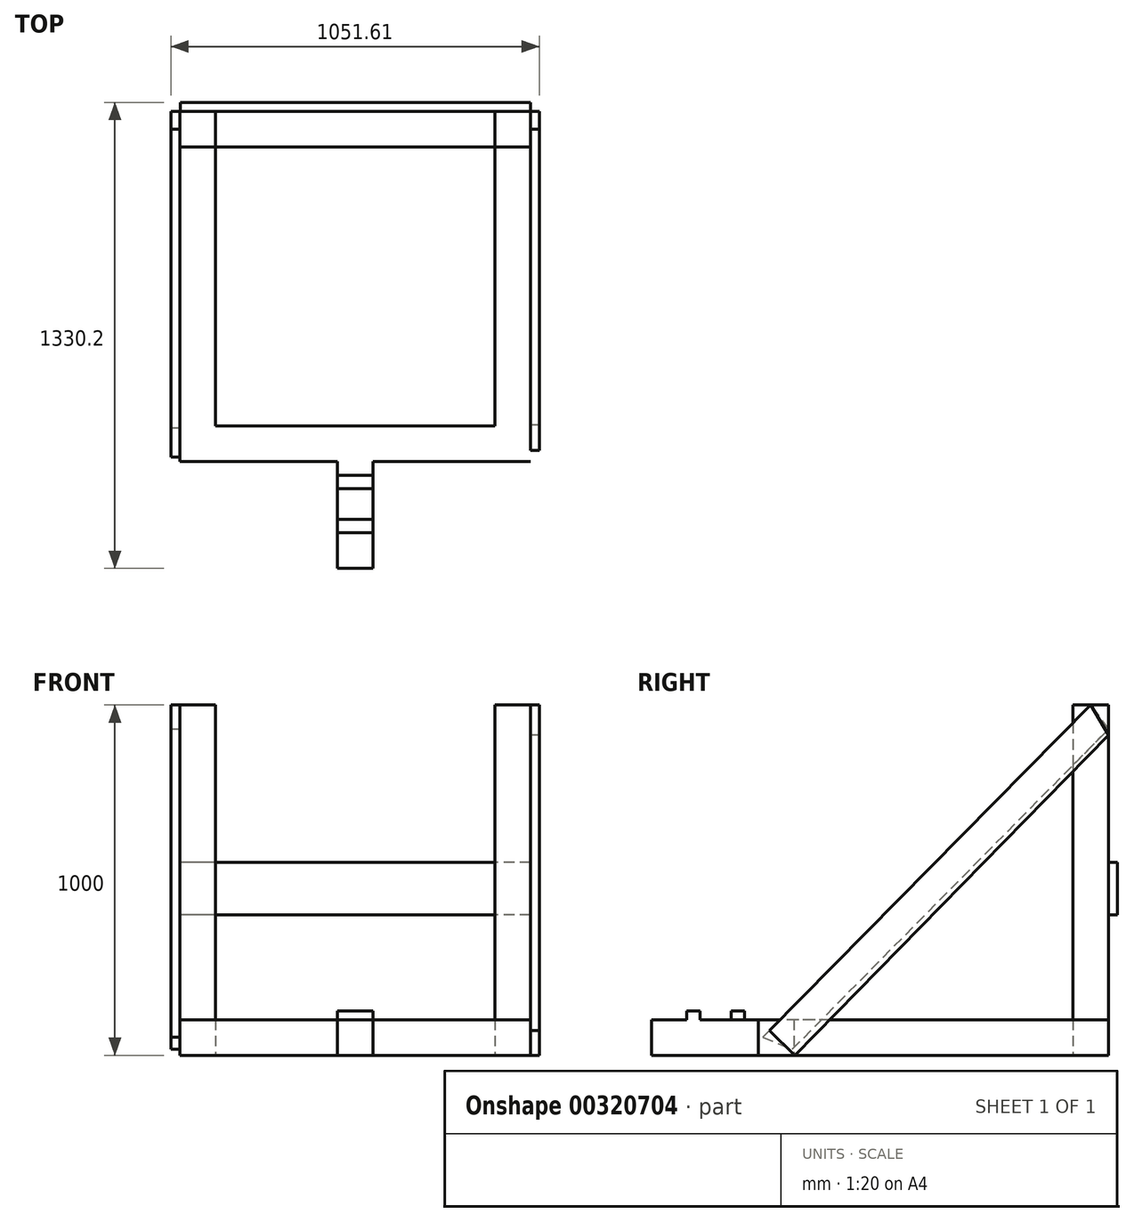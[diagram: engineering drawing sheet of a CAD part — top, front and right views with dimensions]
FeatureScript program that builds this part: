
annotation { "Feature Type Name" : "Feature", "Feature Type Description" : "" }
export const myFeature = defineFeature(function(context is Context, id is Id, definition is map)
    precondition{}
    {
        {
            var Q0;
            Q0=qCreatedBy(makeId("Top.planeOp"),FACE);
            var sketch = newSketch(context, id + "F0", { "sketchPlane" : qUnion([Q0])});
            skLineSegment(sketch, "E0.bottom", {"start": v(-1101.6, 500) * mm, "end": v(-1000, 500) * mm});
            skLineSegment(sketch, "E0.top", {"start": v(-1101.6, -500) * mm, "end": v(-1000, -500) * mm});
            skLineSegment(sketch, "E0.left", {"start": v(-1101.6, 500) * mm, "end": v(-1101.6, -500) * mm});
            skLineSegment(sketch, "E0.right", {"start": v(-1000, 500) * mm, "end": v(-1000, -500) * mm});
            skSolve(sketch);
        }
        {
            var Q0;
            Q0 = qSketchRegion(id + "F0", true);
            extrude(context, id + "F1", {"entities" : qUnion([Q0]), "depth" : 101.6 * mm});
        }
        {
            var Q0;
            Q0=makeQuery(id+"F1.opExtrude","SWEPT_FACE",FACE,{"disambiguationData":[OSD([sQuery(id+"F0.wireOp",EDGE,"E0.right")])]});
            cPlane(context, id + "F2", {"entities" : qUnion([Q0]), "cplaneType" : CPlaneType.OFFSET, "offset" : 0 * mm, "width" : 152.4 * mm, "height" : 152.4 * mm});
        }
        {
            var Q0;
            Q0=qCreatedBy(id+"F2.planeOp",FACE);
            var sketch = newSketch(context, id + "F3", { "sketchPlane" : qUnion([Q0])});
            skLineSegment(sketch, "E1.bottom", {"start": v(500, 101.6) * mm, "end": v(398.4, 101.6) * mm});
            skLineSegment(sketch, "E1.top", {"start": v(500, 0) * mm, "end": v(398.4, 0) * mm});
            skLineSegment(sketch, "E1.left", {"start": v(500, 101.6) * mm, "end": v(500, 0) * mm});
            skLineSegment(sketch, "E1.right", {"start": v(398.4, 101.6) * mm, "end": v(398.4, 0) * mm});
            skSolve(sketch);
        }
        {
            var Q0;
            Q0 = qSketchRegion(id + "F3", true);
            extrude(context, id + "F4", {"entities" : qUnion([Q0]), "operationType" : NewBodyOperationType.ADD, "depth" : 796.8 * mm});
        }
        {
            var Q0;
            Q0=makeQuery(id+"F4.opExtrude","CAP_FACE",FACE,{"disambiguationData":[OSD([sQuery(id+"F3.wireOp",EDGE,"E1.bottom"),sQuery(id+"F3.wireOp",EDGE,"E1.top"),sQuery(id+"F3.wireOp",EDGE,"E1.left"),sQuery(id+"F3.wireOp",EDGE,"E1.right")])],"isStart":false});
            cPlane(context, id + "F5", {"entities" : qUnion([Q0]), "cplaneType" : CPlaneType.OFFSET, "offset" : 0 * mm, "width" : 152.4 * mm, "height" : 152.4 * mm});
        }
        {
            var Q0;
            Q0=qCreatedBy(id+"F5.planeOp",FACE);
            var sketch = newSketch(context, id + "F6", { "sketchPlane" : qUnion([Q0])});
            skLineSegment(sketch, "E2.bottom", {"start": v(500, 101.6) * mm, "end": v(-500, 101.6) * mm});
            skLineSegment(sketch, "E2.top", {"start": v(500, 0) * mm, "end": v(-500, 0) * mm});
            skLineSegment(sketch, "E2.left", {"start": v(500, 101.6) * mm, "end": v(500, 0) * mm});
            skLineSegment(sketch, "E2.right", {"start": v(-500, 101.6) * mm, "end": v(-500, 0) * mm});
            skSolve(sketch);
        }
        {
            var Q0;
            Q0=makeQuery(id+"F6.imprint","IMPRINT",FACE,{"disambiguationData":[TD([[makeQuery(id+"F6.imprint","IMPRINT",EDGE,{"derivedFrom":sQuery(id+"F6.wireOp",EDGE,"E2.bottom")}),1.0]])]});
            extrude(context, id + "F7", {"entities" : qUnion([Q0]), "operationType" : NewBodyOperationType.ADD, "depth" : 101.6 * mm});
        }
        {
            var Q0;
            Q0=makeQuery(id+"F1.opExtrude","SWEPT_FACE",FACE,{"disambiguationData":[OSD([sQuery(id+"F0.wireOp",EDGE,"E0.right")])]});
            var sketch = newSketch(context, id + "F8", { "sketchPlane" : qUnion([Q0])});
            skLineSegment(sketch, "E3.bottom", {"start": v(-500, 101.6) * mm, "end": v(-398.4, 101.6) * mm});
            skLineSegment(sketch, "E3.top", {"start": v(-500, 0) * mm, "end": v(-398.4, 0) * mm});
            skLineSegment(sketch, "E3.left", {"start": v(-500, 101.6) * mm, "end": v(-500, 0) * mm});
            skLineSegment(sketch, "E3.right", {"start": v(-398.4, 101.6) * mm, "end": v(-398.4, 0) * mm});
            skSolve(sketch);
        }
        {
            var Q0;
            Q0 = qSketchRegion(id + "F8", true);
            extrude(context, id + "F9", {"entities" : qUnion([Q0]), "operationType" : NewBodyOperationType.ADD, "depth" : 835.66 * mm});
        }
        {
            var Q0;
            Q0=makeQuery(id+"F9.boolean.opBoolean","MERGE",FACE,{"derivedFrom":[makeQuery(id+"F7.boolean.opBoolean","MERGE",FACE,{"derivedFrom":[makeQuery(id+"F4.boolean.opBoolean","MERGE",FACE,{"derivedFrom":[makeQuery(id+"F1.opExtrude","CAP_FACE",FACE,{"disambiguationData":[OSD([sQuery(id+"F0.wireOp",EDGE,"E0.bottom"),sQuery(id+"F0.wireOp",EDGE,"E0.top"),sQuery(id+"F0.wireOp",EDGE,"E0.left"),sQuery(id+"F0.wireOp",EDGE,"E0.right")])],"isStart":false}),makeQuery(id+"F4.opExtrude","SWEPT_FACE",FACE,{"disambiguationData":[OSD([sQuery(id+"F3.wireOp",EDGE,"E1.bottom")])]})]}),makeQuery(id+"F7.opExtrude","SWEPT_FACE",FACE,{"disambiguationData":[OSD([sQuery(id+"F6.wireOp",EDGE,"E2.bottom")])]})]}),makeQuery(id+"F9.opExtrude","SWEPT_FACE",FACE,{"disambiguationData":[OSD([sQuery(id+"F8.wireOp",EDGE,"E3.bottom")])]})]});
            cPlane(context, id + "F10", {"entities" : qUnion([Q0]), "cplaneType" : CPlaneType.OFFSET, "offset" : 0 * mm, "width" : 152.4 * mm, "height" : 152.4 * mm});
        }
        {
            var Q0;
            Q0=qCreatedBy(id+"F10.planeOp",FACE);
            var sketch = newSketch(context, id + "F11", { "sketchPlane" : qUnion([Q0])});
            skLineSegment(sketch, "E4.bottom", {"start": v(-1102.4, 500) * mm, "end": v(-1000.8, 500) * mm});
            skLineSegment(sketch, "E4.top", {"start": v(-1102.4, 398.4) * mm, "end": v(-1000.8, 398.4) * mm});
            skLineSegment(sketch, "E4.left", {"start": v(-1102.4, 500) * mm, "end": v(-1102.4, 398.4) * mm});
            skLineSegment(sketch, "E4.right", {"start": v(-1000.8, 500) * mm, "end": v(-1000.8, 398.4) * mm});
            skSolve(sketch);
        }
        {
            var Q0;
            Q0 = qSketchRegion(id + "F11", true);
            extrude(context, id + "F12", {"entities" : qUnion([Q0]), "depth" : 898.4 * mm});
        }
        {
            var Q0;
            Q0=qCreatedBy(id+"F10.planeOp",FACE);
            var sketch = newSketch(context, id + "F13", { "sketchPlane" : qUnion([Q0])});
            skLineSegment(sketch, "E5.bottom", {"start": v(-203.2, 500) * mm, "end": v(-101.6, 500) * mm});
            skLineSegment(sketch, "E5.top", {"start": v(-203.2, 398.4) * mm, "end": v(-101.6, 398.4) * mm});
            skLineSegment(sketch, "E5.left", {"start": v(-203.2, 500) * mm, "end": v(-203.2, 398.4) * mm});
            skLineSegment(sketch, "E5.right", {"start": v(-101.6, 500) * mm, "end": v(-101.6, 398.4) * mm});
            skSolve(sketch);
        }
        {
            var Q0;
            Q0 = qSketchRegion(id + "F13", true);
            extrude(context, id + "F14", {"entities" : qUnion([Q0]), "depth" : 898.4 * mm});
        }
        {
            var Q0;
            Q0=makeQuery(id+"F14.opExtrude","SWEPT_FACE",FACE,{"disambiguationData":[OSD([sQuery(id+"F13.wireOp",EDGE,"E5.right")])]});
            var sketch = newSketch(context, id + "F15", { "sketchPlane" : qUnion([Q0])});
            skLineSegment(sketch, "E6", {"start": v(500, 913.36) * mm, "end": v(-395.72, 0) * mm});
            skLineSegment(sketch, "E7", {"start": v(-395.72, 0) * mm, "end": v(-468.25, 71.13) * mm});
            skLineSegment(sketch, "E8", {"start": v(-468.25, 71.13) * mm, "end": v(449.2, 1000) * mm});
            skLineSegment(sketch, "E9", {"start": v(449.2, 1000) * mm, "end": v(500, 913.36) * mm});
            skSolve(sketch);
        }
        {
            var Q0;
            {var subQ0=sQuery(id+"F15.wireOp",EDGE,"E9");Q0=makeQuery(id+"F15.imprint","IMPRINT",FACE,{"disambiguationData":[TD([[makeQuery(id+"F15.imprint","IMPRINT",EDGE,{"derivedFrom":subQ0}),-1.0]])]});}
            var Q1;
            {var subQ0=sQuery(id+"F15.wireOp",EDGE,"E7");Q1=makeQuery(id+"F15.imprint","IMPRINT",FACE,{"disambiguationData":[TD([[makeQuery(id+"F15.imprint","IMPRINT",EDGE,{"derivedFrom":subQ0}),-1.0]])]});}
            extrude(context, id + "F16", {"entities" : qUnion([Q0, Q1]), "depth" : 25.4 * mm});
        }
        {
            var Q0;
            Q0=makeQuery(id+"F12.opExtrude","SWEPT_FACE",FACE,{"disambiguationData":[OSD([sQuery(id+"F11.wireOp",EDGE,"E4.left")])]});
            var sketch = newSketch(context, id + "F17", { "sketchPlane" : qUnion([Q0])});
            skLineSegment(sketch, "E10", {"start": v(-449.2, 1000) * mm, "end": v(486.85, 52.13) * mm});
            skLineSegment(sketch, "E11", {"start": v(486.85, 52.13) * mm, "end": v(402.9, 16.88) * mm});
            skLineSegment(sketch, "E12", {"start": v(402.9, 16.88) * mm, "end": v(-500, 931.19) * mm});
            skLineSegment(sketch, "E13", {"start": v(-500, 931.19) * mm, "end": v(-449.2, 1000) * mm});
            skSolve(sketch);
        }
        {
            var Q0;
            {var subQ0=sQuery(id+"F17.wireOp",EDGE,"E11");Q0=makeQuery(id+"F17.imprint","IMPRINT",FACE,{"disambiguationData":[TD([[makeQuery(id+"F17.imprint","IMPRINT",EDGE,{"derivedFrom":subQ0}),-1.0]])]});}
            var Q1;
            {var subQ0=sQuery(id+"F17.wireOp",EDGE,"E13");Q1=makeQuery(id+"F17.imprint","IMPRINT",FACE,{"disambiguationData":[TD([[makeQuery(id+"F17.imprint","IMPRINT",EDGE,{"derivedFrom":subQ0}),-1.0]])]});}
            extrude(context, id + "F18", {"entities" : qUnion([Q0, Q1]), "operationType" : NewBodyOperationType.ADD, "depth" : 25.4 * mm});
        }
        {
            var Q0;
            Q0=makeQuery(id+"F9.boolean.opBoolean","MERGE",FACE,{"derivedFrom":[makeQuery(id+"F7.boolean.opBoolean","MERGE",FACE,{"derivedFrom":[makeQuery(id+"F4.boolean.opBoolean","MERGE",FACE,{"derivedFrom":[makeQuery(id+"F1.opExtrude","CAP_FACE",FACE,{"disambiguationData":[OSD([sQuery(id+"F0.wireOp",EDGE,"E0.bottom"),sQuery(id+"F0.wireOp",EDGE,"E0.top"),sQuery(id+"F0.wireOp",EDGE,"E0.left"),sQuery(id+"F0.wireOp",EDGE,"E0.right")])],"isStart":false}),makeQuery(id+"F4.opExtrude","SWEPT_FACE",FACE,{"disambiguationData":[OSD([sQuery(id+"F3.wireOp",EDGE,"E1.bottom")])]})]}),makeQuery(id+"F7.opExtrude","SWEPT_FACE",FACE,{"disambiguationData":[OSD([sQuery(id+"F6.wireOp",EDGE,"E2.bottom")])]})]}),makeQuery(id+"F9.opExtrude","SWEPT_FACE",FACE,{"disambiguationData":[OSD([sQuery(id+"F8.wireOp",EDGE,"E3.bottom")])]})]});
            var sketch = newSketch(context, id + "F19", { "sketchPlane" : qUnion([Q0])});
            skLineSegment(sketch, "E14.bottom", {"start": v(-964.58, 2068.75) * mm, "end": v(558.18, 2068.75) * mm});
            skLineSegment(sketch, "E14.top", {"start": v(-964.58, -1271.95) * mm, "end": v(558.18, -1271.95) * mm});
            skLineSegment(sketch, "E14.left", {"start": v(-964.58, 2068.75) * mm, "end": v(-964.58, -1271.95) * mm});
            skLineSegment(sketch, "E14.right", {"start": v(558.18, 2068.75) * mm, "end": v(558.18, -1271.95) * mm});
            skPoint(sketch, "E14.middle", {"position": v(-203.2, 398.4) * mm});
            skSolve(sketch);
        }
        {
            var Q0;
            Q0=makeQuery(id+"F9.boolean.opBoolean","MERGE",FACE,{"derivedFrom":[makeQuery(id+"F1.opExtrude","SWEPT_FACE",FACE,{"disambiguationData":[OSD([sQuery(id+"F0.wireOp",EDGE,"E0.top")])]}),makeQuery(id+"F7.opExtrude","SWEPT_FACE",FACE,{"disambiguationData":[OSD([sQuery(id+"F6.wireOp",EDGE,"E2.right")])]}),makeQuery(id+"F9.opExtrude","SWEPT_FACE",FACE,{"disambiguationData":[OSD([sQuery(id+"F8.wireOp",EDGE,"E3.left")])]})]});
            var sketch = newSketch(context, id + "F20", { "sketchPlane" : qUnion([Q0])});
            skLineSegment(sketch, "E15.bottom", {"start": v(-550.8, 0) * mm, "end": v(-652.4, 0) * mm});
            skLineSegment(sketch, "E15.top", {"start": v(-550.8, 101.6) * mm, "end": v(-652.4, 101.6) * mm});
            skLineSegment(sketch, "E15.left", {"start": v(-550.8, 0) * mm, "end": v(-550.8, 101.6) * mm});
            skLineSegment(sketch, "E15.right", {"start": v(-652.4, 0) * mm, "end": v(-652.4, 101.6) * mm});
            skPoint(sketch, "E15.middle", {"position": v(-601.6, 50.8) * mm});
            skPoint(sketch, "E15.middle.positionSnap0", {"position": v(-601.6, 101.6) * mm});
            skPoint(sketch, "E15.centerSnap0", {"position": v(-601.6, 101.6) * mm});
            skSolve(sketch);
        }
        {
            var Q0;
            Q0 = qSketchRegion(id + "F20", true);
            extrude(context, id + "F21", {"entities" : qUnion([Q0]), "operationType" : NewBodyOperationType.ADD, "depth" : 304.8 * mm});
        }
        {
            var Q0;
            {var subQ1=sQuery(id+"F19.wireOp",EDGE,"E14.bottom");Q0=makeQuery(id+"F19.imprint","IMPRINT",FACE,{"disambiguationData":[TD([[makeQuery(id+"F19.imprint","IMPRINT",EDGE,{"derivedFrom":subQ1}),-1.0]])]});}
            var sketch = newSketch(context, id + "F22", { "sketchPlane" : qUnion([Q0])});
            skLineSegment(sketch, "E16.bottom", {"start": v(-652.21, -577.66) * mm, "end": v(-550.99, -577.66) * mm});
            skLineSegment(sketch, "E16.top", {"start": v(-652.21, -539.56) * mm, "end": v(-550.99, -539.56) * mm});
            skLineSegment(sketch, "E16.left", {"start": v(-652.21, -577.66) * mm, "end": v(-652.21, -539.56) * mm});
            skLineSegment(sketch, "E16.right", {"start": v(-550.99, -577.66) * mm, "end": v(-550.99, -539.56) * mm});
            skPoint(sketch, "E16.middle", {"position": v(-601.6, -558.6) * mm});
            skSolve(sketch);
        }
        {
            var Q0;
            Q0 = qSketchRegion(id + "F22", true);
            extrude(context, id + "F23", {"entities" : qUnion([Q0]), "operationType" : NewBodyOperationType.ADD, "depth" : 25.4 * mm});
        }
        {
            var Q0;
            {var subQ1=sQuery(id+"F19.wireOp",EDGE,"E14.bottom");Q0=makeQuery(id+"F19.imprint","IMPRINT",FACE,{"disambiguationData":[TD([[makeQuery(id+"F19.imprint","IMPRINT",EDGE,{"derivedFrom":subQ1}),-1.0]])]});}
            var sketch = newSketch(context, id + "F24", { "sketchPlane" : qUnion([Q0])});
            skLineSegment(sketch, "E17.bottom", {"start": v(-652.4, -703.64) * mm, "end": v(-550.8, -703.64) * mm});
            skLineSegment(sketch, "E17.top", {"start": v(-652.4, -665.54) * mm, "end": v(-550.8, -665.54) * mm});
            skLineSegment(sketch, "E17.left", {"start": v(-652.4, -703.64) * mm, "end": v(-652.4, -665.54) * mm});
            skLineSegment(sketch, "E17.right", {"start": v(-550.8, -703.64) * mm, "end": v(-550.8, -665.54) * mm});
            skPoint(sketch, "E17.middle", {"position": v(-601.6, -684.59) * mm});
            skSolve(sketch);
        }
        {
            var Q0;
            Q0 = qSketchRegion(id + "F24", true);
            extrude(context, id + "F25", {"entities" : qUnion([Q0]), "operationType" : NewBodyOperationType.ADD, "depth" : 25.4 * mm});
        }
        {
            var Q0;
            Q0=makeQuery(id+"F14.opExtrude","SWEPT_FACE",FACE,{"disambiguationData":[OSD([sQuery(id+"F13.wireOp",EDGE,"E5.bottom")])]});
            var sketch = newSketch(context, id + "F26", { "sketchPlane" : qUnion([Q0])});
            skLineSegment(sketch, "E18.bottom", {"start": v(101.6, 550.8) * mm, "end": v(1100.3, 550.8) * mm});
            skLineSegment(sketch, "E18.top", {"start": v(101.6, 400.54) * mm, "end": v(1100.3, 400.54) * mm});
            skLineSegment(sketch, "E18.left", {"start": v(101.6, 550.8) * mm, "end": v(101.6, 400.54) * mm});
            skLineSegment(sketch, "E18.right", {"start": v(1100.3, 550.8) * mm, "end": v(1100.3, 400.54) * mm});
            skSolve(sketch);
        }
        {
            var Q0;
            Q0 = qSketchRegion(id + "F26", true);
            extrude(context, id + "F27", {"entities" : qUnion([Q0]), "depth" : 25.4 * mm});
        }
    });
